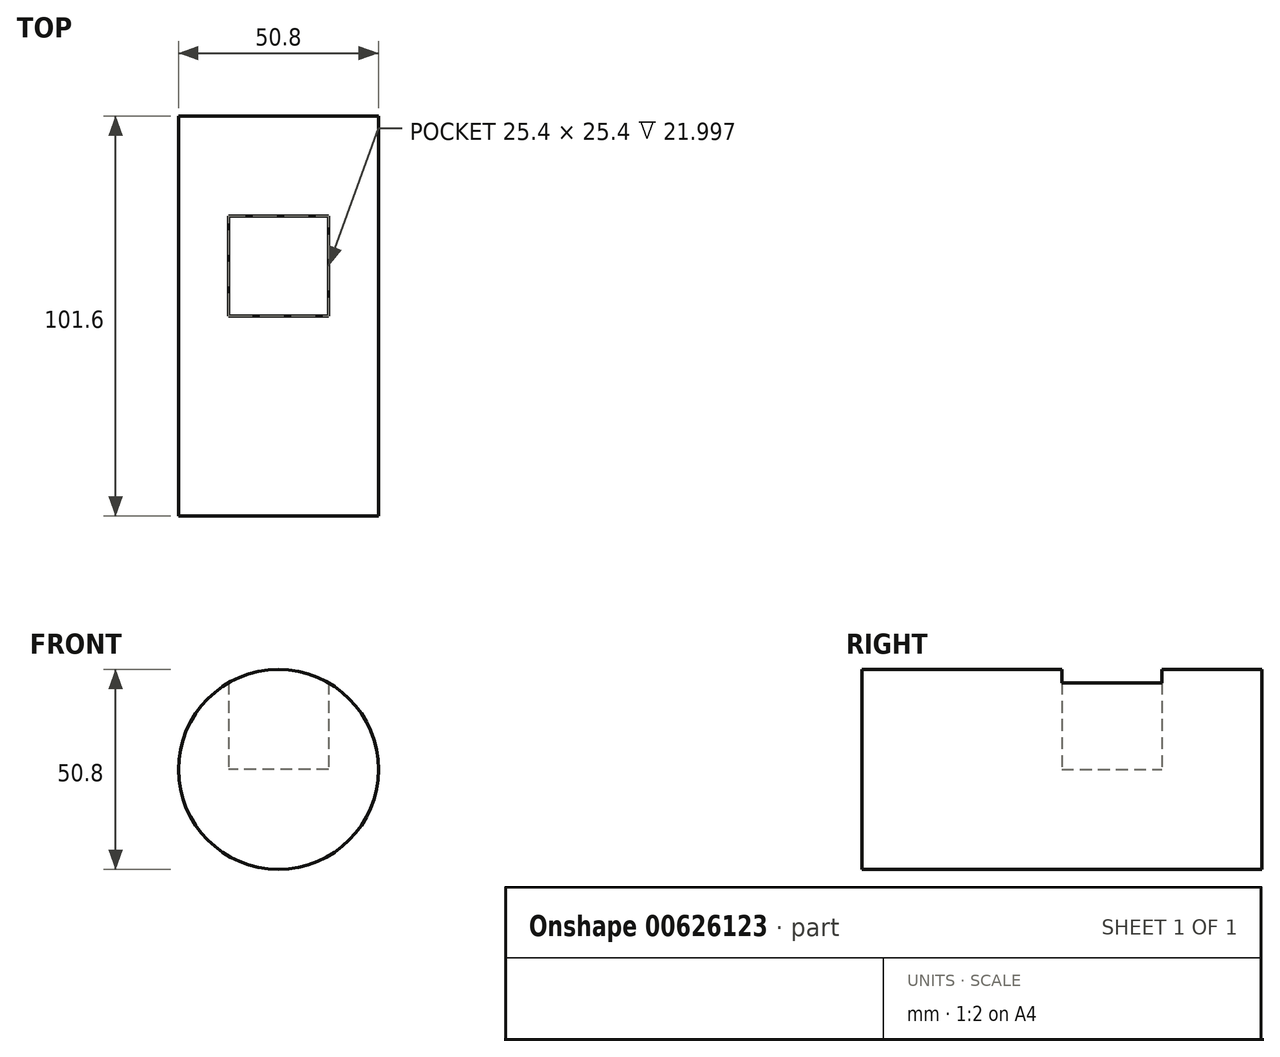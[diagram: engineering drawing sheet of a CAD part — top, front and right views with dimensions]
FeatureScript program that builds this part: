
annotation { "Feature Type Name" : "Feature", "Feature Type Description" : "" }
export const myFeature = defineFeature(function(context is Context, id is Id, definition is map)
    precondition{}
    {
        {
            var Q0;
            Q0=qCreatedBy(makeId("Front.planeOp"),FACE);
            var sketch = newSketch(context, id + "F0", { "sketchPlane" : qUnion([Q0])});
            skCircle(sketch, "E0", {"center": v(0, 0) * mm, "radius": 25.4 * mm});
            skSolve(sketch);
        }
        {
            var Q0;
            Q0 = qSketchRegion(id + "F0", false);
            extrude(context, id + "F1", {"entities" : qUnion([Q0]), "depth" : 101.6 * mm});
        }
        {
            var Q0;
            Q0=qCreatedBy(makeId("Top.planeOp"),FACE);
            var sketch = newSketch(context, id + "F2", { "sketchPlane" : qUnion([Q0])});
            skLineSegment(sketch, "E1.bottom", {"start": v(12.7, -50.8) * mm, "end": v(-12.7, -50.8) * mm});
            skLineSegment(sketch, "E1.top", {"start": v(12.7, -25.4) * mm, "end": v(-12.7, -25.4) * mm});
            skLineSegment(sketch, "E1.left", {"start": v(12.7, -50.8) * mm, "end": v(12.7, -25.4) * mm});
            skLineSegment(sketch, "E1.right", {"start": v(-12.7, -50.8) * mm, "end": v(-12.7, -25.4) * mm});
            skLineSegment(sketch, "E2", {"start": v(0, -25.4) * mm, "end": v(0, 0) * mm});
            skSolve(sketch);
        }
        {
            var Q0;
            Q0 = qSketchRegion(id + "F2", false);
            extrude(context, id + "F3", {"entities" : qUnion([Q0]), "operationType" : NewBodyOperationType.REMOVE, "endBound" : BoundingType.UP_TO_NEXT, "hasSecondDirection" : true, "secondDirectionOppositeDirection" : false, "secondDirectionDepth" : 0 * mm});
        }
    });
